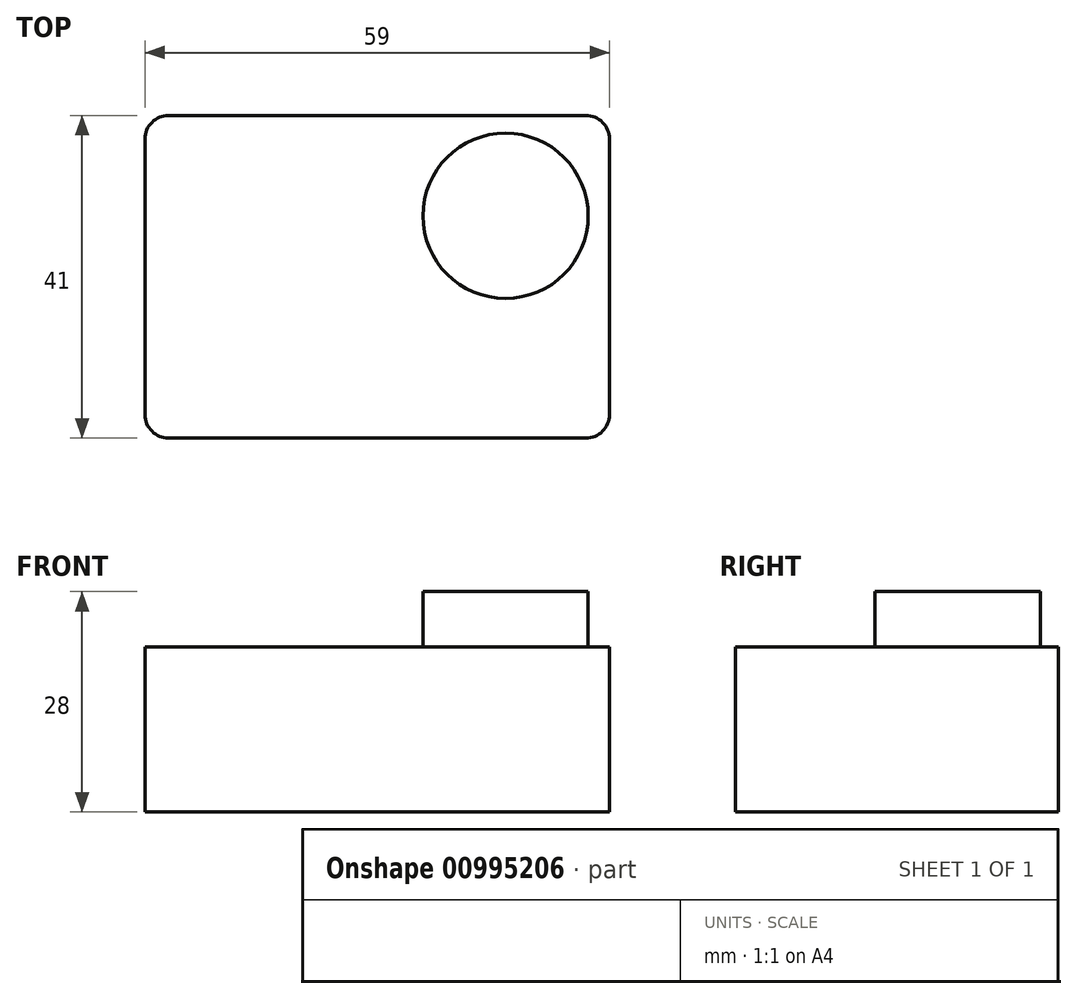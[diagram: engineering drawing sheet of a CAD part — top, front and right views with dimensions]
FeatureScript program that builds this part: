
annotation { "Feature Type Name" : "Feature", "Feature Type Description" : "" }
export const myFeature = defineFeature(function(context is Context, id is Id, definition is map)
    precondition{}
    {
        {
            var Q0;
            Q0=qCreatedBy(makeId("Top.planeOp"),FACE);
            var sketch = newSketch(context, id + "F0", { "sketchPlane" : qUnion([Q0])});
            skLineSegment(sketch, "E0.bottom", {"start": v(29.5, -20.5) * mm, "end": v(-29.5, -20.5) * mm});
            skLineSegment(sketch, "E0.top", {"start": v(29.5, 20.5) * mm, "end": v(-29.5, 20.5) * mm});
            skLineSegment(sketch, "E0.left", {"start": v(29.5, -20.5) * mm, "end": v(29.5, 20.5) * mm});
            skLineSegment(sketch, "E0.right", {"start": v(-29.5, -20.5) * mm, "end": v(-29.5, 20.5) * mm});
            skPoint(sketch, "E0.middle", {"position": v(0, 0) * mm});
            skSolve(sketch);
        }
        {
            var Q0;
            Q0=makeQuery(id+"F0.imprint","IMPRINT",FACE,{"disambiguationData":[TD([[makeQuery(id+"F0.imprint","IMPRINT",EDGE,{"derivedFrom":sQuery(id+"F0.wireOp",EDGE,"E0.bottom")}),-1.0]])]});
            extrude(context, id + "F1", {"entities" : qUnion([Q0]), "depth" : 21 * mm, "offsetDistance" : 25 * mm});
        }
        {
            var Q0;
            Q0=makeQuery(id+"F1.opExtrude","SWEPT_EDGE",EDGE,{"disambiguationData":[OSD([sQuery(id+"F0.wireOp",EDGE,"E0.bottom"),sQuery(id+"F0.wireOp",EDGE,"E0.right")])]});
            var Q1;
            Q1=makeQuery(id+"F1.opExtrude","SWEPT_EDGE",EDGE,{"disambiguationData":[OSD([sQuery(id+"F0.wireOp",EDGE,"E0.top"),sQuery(id+"F0.wireOp",EDGE,"E0.right")])]});
            var Q2;
            Q2=makeQuery(id+"F1.opExtrude","SWEPT_EDGE",EDGE,{"disambiguationData":[OSD([sQuery(id+"F0.wireOp",EDGE,"E0.bottom"),sQuery(id+"F0.wireOp",EDGE,"E0.left")])]});
            var Q3;
            Q3=makeQuery(id+"F1.opExtrude","SWEPT_EDGE",EDGE,{"disambiguationData":[OSD([sQuery(id+"F0.wireOp",EDGE,"E0.top"),sQuery(id+"F0.wireOp",EDGE,"E0.left")])]});
            fillet(context, id + "F2", {"entities" : qUnion([Q0, Q1, Q2, Q3]), "radius" : 3 * mm, "tangentPropagation" : true, "allowEdgeOverflow" : false});
        }
        {
            var Q0;
            Q0=makeQuery(id+"F1.opExtrude","CAP_FACE",FACE,{"disambiguationData":[OSD([sQuery(id+"F0.wireOp",EDGE,"E0.bottom"),sQuery(id+"F0.wireOp",EDGE,"E0.top"),sQuery(id+"F0.wireOp",EDGE,"E0.left"),sQuery(id+"F0.wireOp",EDGE,"E0.right")])],"isStart":false});
            var sketch = newSketch(context, id + "F3", { "sketchPlane" : qUnion([Q0])});
            skCircle(sketch, "E1", {"center": v(16.3, 7.75) * mm, "radius": 10.5 * mm});
            skSolve(sketch);
        }
        {
            var Q0;
            Q0=makeQuery(id+"F3.imprint","IMPRINT",FACE,{"disambiguationData":[TD([[makeQuery(id+"F3.imprint","IMPRINT",EDGE,{"derivedFrom":sQuery(id+"F3.wireOp",EDGE,"E1")}),1.0]])]});
            extrude(context, id + "F4", {"entities" : qUnion([Q0]), "operationType" : NewBodyOperationType.ADD, "depth" : 7 * mm, "offsetDistance" : 25 * mm});
        }
    });
